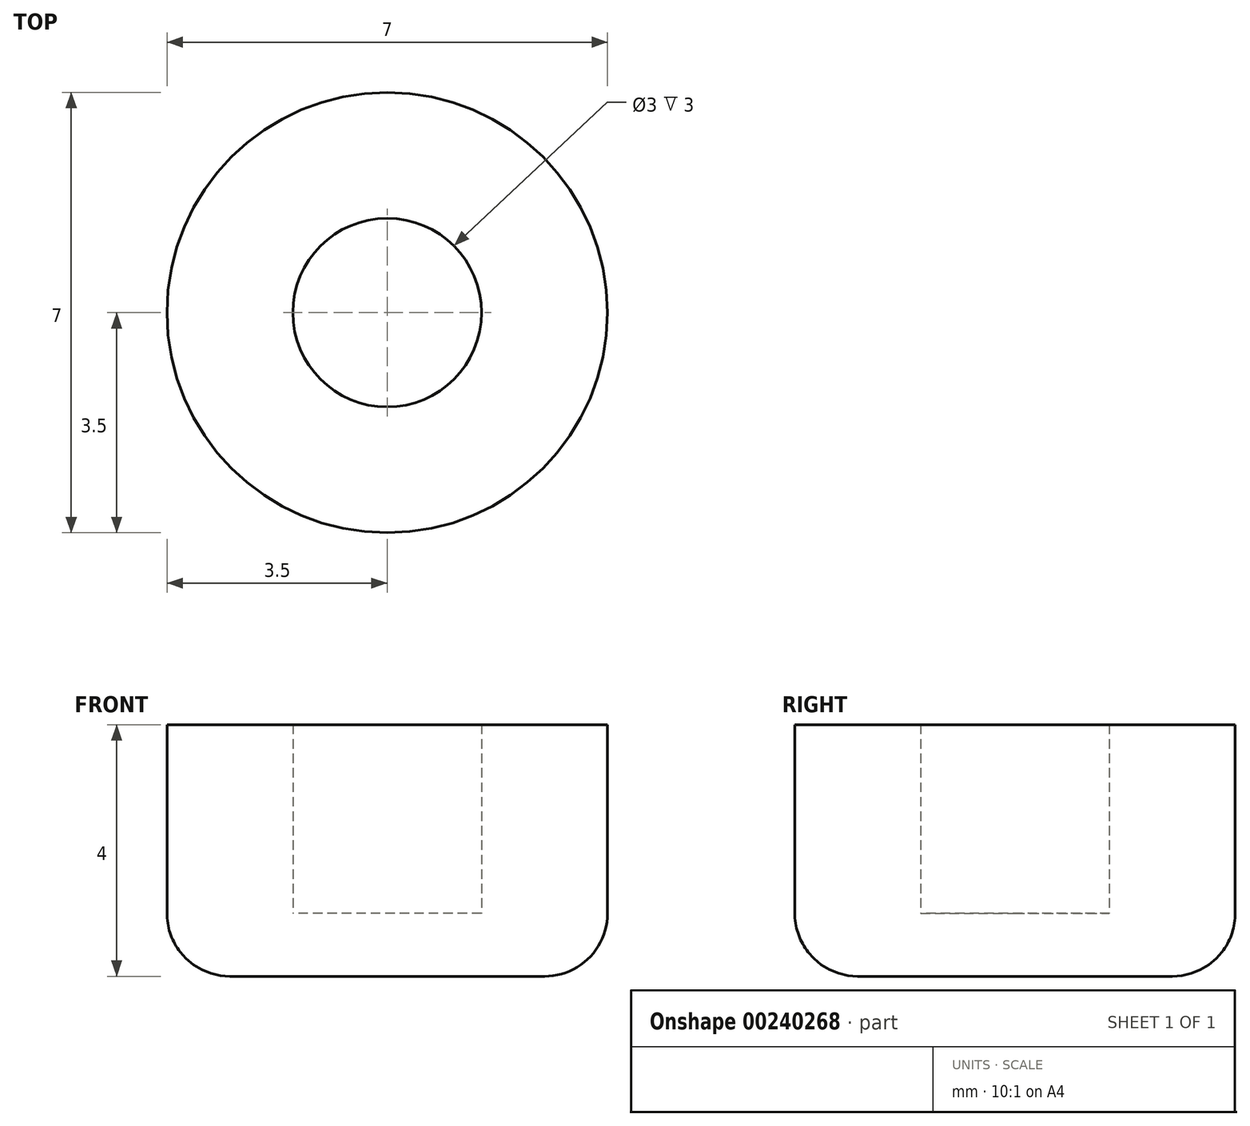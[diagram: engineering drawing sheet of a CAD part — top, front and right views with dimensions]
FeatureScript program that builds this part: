
annotation { "Feature Type Name" : "Feature", "Feature Type Description" : "" }
export const myFeature = defineFeature(function(context is Context, id is Id, definition is map)
    precondition{}
    {
        {
            var Q0;
            Q0=qCreatedBy(makeId("Top.planeOp"),FACE);
            var sketch = newSketch(context, id + "F0", { "sketchPlane" : qUnion([Q0])});
            skCircle(sketch, "E0", {"center": v(0, 0) * mm, "radius": 1.5 * mm});
            skCircle(sketch, "E1.0", {"center": v(0, 0) * mm, "radius": 3.5 * mm});
            skSolve(sketch);
        }
        {
            var Q0;
            Q0 = qSketchRegion(id + "F0", true);
            extrude(context, id + "F1", {"entities" : qUnion([Q0]), "depth" : 3 * mm});
        }
        {
            var Q0;
            Q0=qCreatedBy(makeId("Top.planeOp"),FACE);
            var sketch = newSketch(context, id + "F2", { "sketchPlane" : qUnion([Q0])});
            skCircle(sketch, "E2.0", {"center": v(0, 0) * mm, "radius": 3.5 * mm});
            skSolve(sketch);
        }
        {
            var Q0;
            Q0 = qSketchRegion(id + "F2", true);
            extrude(context, id + "F3", {"entities" : qUnion([Q0]), "operationType" : NewBodyOperationType.ADD, "oppositeDirection" : true, "depth" : 1 * mm});
        }
        {
            var Q0;
            Q0=makeQuery(id+"F3.opExtrude","CAP_EDGE",EDGE,{"disambiguationData":[OSD([sQuery(id+"F2.wireOp",EDGE,"E2.0")])],"isStart":false});
            fillet(context, id + "F4", {"entities" : qUnion([Q0]), "radius" : 1 * mm, "tangentPropagation" : true, "allowEdgeOverflow" : false});
        }
    });
